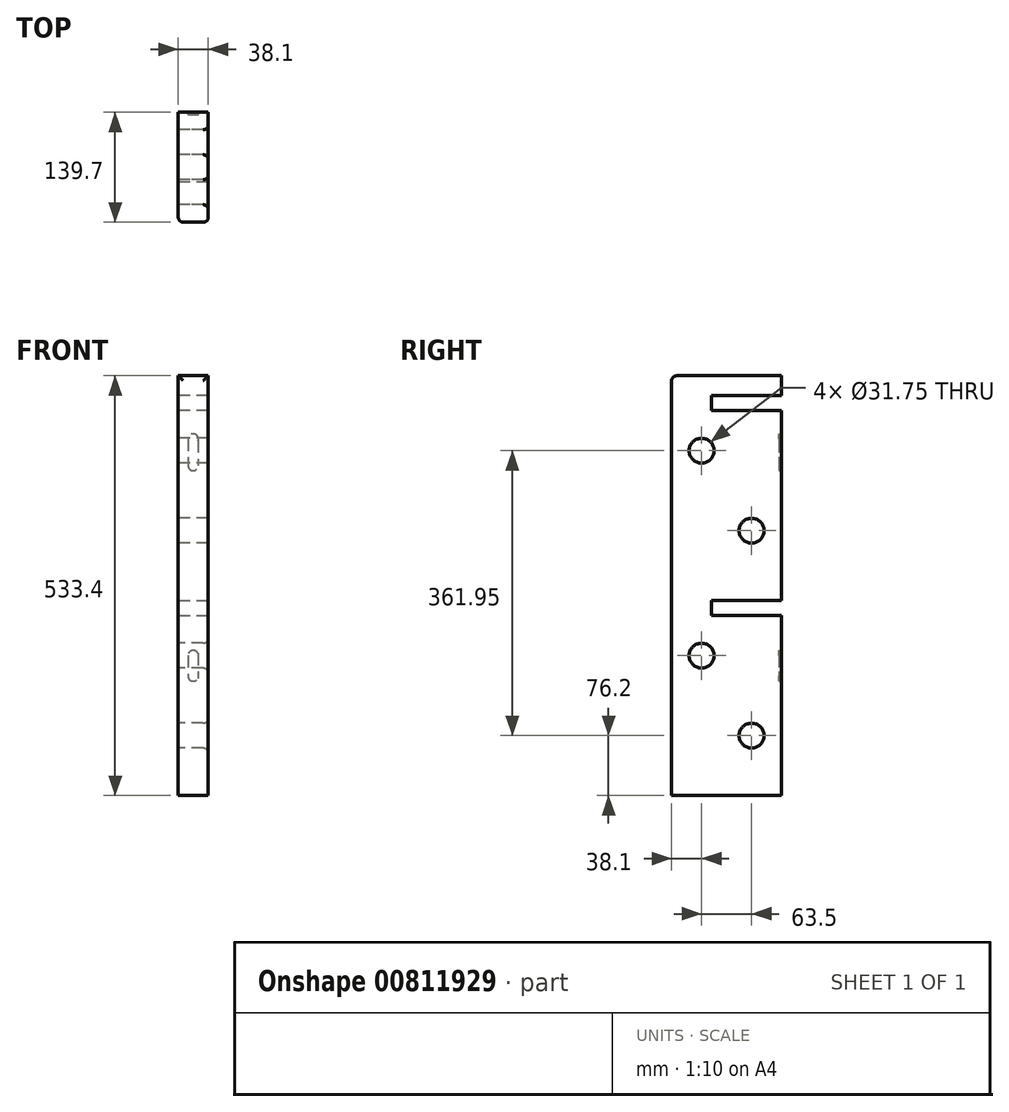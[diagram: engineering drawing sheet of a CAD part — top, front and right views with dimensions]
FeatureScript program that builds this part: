
annotation { "Feature Type Name" : "Feature", "Feature Type Description" : "" }
export const myFeature = defineFeature(function(context is Context, id is Id, definition is map)
    precondition{}
    {
        {
            var Q0;
            Q0=qCreatedBy(makeId("Front.planeOp"),FACE);
            var sketch = newSketch(context, id + "F0", { "sketchPlane" : qUnion([Q0])});
            skLineSegment(sketch, "E0.bottom", {"start": v(-19.05, 304.8) * mm, "end": v(19.05, 304.8) * mm});
            skLineSegment(sketch, "E0.top", {"start": v(-19.05, -304.8) * mm, "end": v(19.05, -304.8) * mm});
            skLineSegment(sketch, "E0.left", {"start": v(-19.05, 304.8) * mm, "end": v(-19.05, -304.8) * mm});
            skLineSegment(sketch, "E0.right", {"start": v(19.05, 304.8) * mm, "end": v(19.05, -304.8) * mm});
            skSolve(sketch);
        }
        {
            var Q0;
            Q0 = qSketchRegion(id + "F0", true);
            extrude(context, id + "F1", {"entities" : qUnion([Q0]), "depth" : 69.85 * mm, "offsetDistance" : 25.4 * mm, "hasSecondDirection" : true, "secondDirectionOppositeDirection" : true, "secondDirectionDepth" : 69.85 * mm});
        }
        {
            var Q0;
            Q0=makeQuery(id+"F1.opExtrude","SWEPT_FACE",FACE,{"disambiguationData":[OSD([sQuery(id+"F0.wireOp",EDGE,"E0.left")])]});
            var sketch = newSketch(context, id + "F2", { "sketchPlane" : qUnion([Q0])});
            skLineSegment(sketch, "E1.bottom", {"start": v(-69.85, 279.4) * mm, "end": v(19.05, 279.4) * mm});
            skLineSegment(sketch, "E1.top", {"start": v(-69.85, 260.35) * mm, "end": v(19.05, 260.35) * mm});
            skLineSegment(sketch, "E1.left", {"start": v(-69.85, 279.4) * mm, "end": v(-69.85, 260.35) * mm});
            skLineSegment(sketch, "E1.right", {"start": v(19.05, 279.4) * mm, "end": v(19.05, 260.35) * mm});
            skSolve(sketch);
        }
        {
            var Q0;
            Q0=makeQuery(id+"F2.imprint","IMPRINT",FACE,{"disambiguationData":[TD([[makeQuery(id+"F2.imprint","IMPRINT",EDGE,{"derivedFrom":sQuery(id+"F2.wireOp",EDGE,"E1.bottom")}),-1.0]])]});
            extrude(context, id + "F3", {"entities" : qUnion([Q0]), "operationType" : NewBodyOperationType.REMOVE, "oppositeDirection" : true, "depth" : 38.1 * mm, "offsetDistance" : 25.4 * mm});
        }
        {
            var Q0;
            Q0=makeQuery(id+"F1.opExtrude","SWEPT_FACE",FACE,{"disambiguationData":[OSD([sQuery(id+"F0.wireOp",EDGE,"E0.left")])]});
            var sketch = newSketch(context, id + "F4", { "sketchPlane" : qUnion([Q0])});
            skLineSegment(sketch, "E2", {"start": v(31.75, 304.8) * mm, "end": v(31.75, -304.8) * mm});
            skLineSegment(sketch, "E3", {"start": v(-31.75, 260.35) * mm, "end": v(-31.75, -304.8) * mm});
            skSolve(sketch);
        }
        {
            var Q0;
            {var subQ3=sQuery(id+"F4.wireOp",EDGE,"E2");Q0=makeQuery(id+"F4.imprint","IMPRINT",FACE,{"disambiguationData":[TD([[makeQuery(id+"F4.imprint","IMPRINT",EDGE,{"derivedFrom":subQ3}),-1.0]])]});}
            var sketch = newSketch(context, id + "F5", { "sketchPlane" : qUnion([Q0])});
            skCircle(sketch, "E4", {"center": v(31.75, 209.55) * mm, "radius": 15.88 * mm});
            skCircle(sketch, "E5", {"center": v(-31.75, 107.95) * mm, "radius": 15.88 * mm});
            skCircle(sketch, "E6", {"center": v(31.75, -50.8) * mm, "radius": 15.88 * mm});
            skCircle(sketch, "E7", {"center": v(-31.75, -152.4) * mm, "radius": 15.88 * mm});
            skSolve(sketch);
        }
        {
            var Q0;
            Q0 = qSketchRegion(id + "F5", true);
            extrude(context, id + "F6", {"entities" : qUnion([Q0]), "operationType" : NewBodyOperationType.REMOVE, "oppositeDirection" : true, "depth" : 50.8 * mm, "offsetDistance" : 25.4 * mm});
        }
        {
            var Q0;
            Q0=makeQuery(id+"F1.opExtrude","SWEPT_FACE",FACE,{"disambiguationData":[OSD([sQuery(id+"F0.wireOp",EDGE,"E0.right")])]});
            var sketch = newSketch(context, id + "F7", { "sketchPlane" : qUnion([Q0])});
            skLineSegment(sketch, "E8.bottom", {"start": v(69.85, 19.05) * mm, "end": v(-19.05, 19.05) * mm});
            skLineSegment(sketch, "E8.top", {"start": v(69.85, 0) * mm, "end": v(-19.05, 0) * mm});
            skLineSegment(sketch, "E8.left", {"start": v(69.85, 19.05) * mm, "end": v(69.85, 0) * mm});
            skLineSegment(sketch, "E8.right", {"start": v(-19.05, 19.05) * mm, "end": v(-19.05, 0) * mm});
            skLineSegment(sketch, "E9.bottom", {"start": v(69.85, -228.6) * mm, "end": v(-69.85, -228.6) * mm});
            skLineSegment(sketch, "E9.top", {"start": v(69.85, -304.8) * mm, "end": v(-69.85, -304.8) * mm});
            skLineSegment(sketch, "E9.left", {"start": v(69.85, -228.6) * mm, "end": v(69.85, -304.8) * mm});
            skLineSegment(sketch, "E9.right", {"start": v(-69.85, -228.6) * mm, "end": v(-69.85, -304.8) * mm});
            skSolve(sketch);
        }
        {
            var Q0;
            Q0 = qSketchRegion(id + "F7", true);
            extrude(context, id + "F8", {"entities" : qUnion([Q0]), "operationType" : NewBodyOperationType.REMOVE, "endBound" : BoundingType.UP_TO_NEXT, "oppositeDirection" : true, "depth" : 25.4 * mm, "offsetDistance" : 25.4 * mm});
        }
        {
            var Q0;
            Q0=makeQuery(id+"F6.boolean.opBoolean","COPY",EDGE,{"derivedFrom":makeQuery(id+"F6.opExtrude","CAP_EDGE",EDGE,{"disambiguationData":[OSD([sQuery(id+"F5.wireOp",EDGE,"E4")])],"isStart":true})});
            var Q1;
            Q1=makeQuery(id+"F6.boolean.opBoolean","COPY",EDGE,{"derivedFrom":makeQuery(id+"F6.opExtrude","CAP_EDGE",EDGE,{"disambiguationData":[OSD([sQuery(id+"F5.wireOp",EDGE,"E5")])],"isStart":true})});
            var Q2;
            Q2=makeQuery(id+"F6.boolean.opBoolean","INTERSECT",EDGE,{"derivedFrom":[makeQuery(id+"F1.opExtrude","SWEPT_FACE",FACE,{"disambiguationData":[OSD([sQuery(id+"F0.wireOp",EDGE,"E0.right")])]}),makeQuery(id+"F6.opExtrude","SWEPT_FACE",FACE,{"disambiguationData":[OSD([sQuery(id+"F5.wireOp",EDGE,"E6")])]})]});
            var Q3;
            Q3=makeQuery(id+"F6.boolean.opBoolean","INTERSECT",EDGE,{"derivedFrom":[makeQuery(id+"F1.opExtrude","SWEPT_FACE",FACE,{"disambiguationData":[OSD([sQuery(id+"F0.wireOp",EDGE,"E0.right")])]}),makeQuery(id+"F6.opExtrude","SWEPT_FACE",FACE,{"disambiguationData":[OSD([sQuery(id+"F5.wireOp",EDGE,"E7")])]})]});
            fillet(context, id + "F9", {"entities" : qUnion([Q0, Q1, Q2, Q3]), "radius" : 6.35 * mm, "tangentPropagation" : true, "allowEdgeOverflow" : false});
        }
        {
            var Q0;
            {var subQ0=sQuery(id+"F0.wireOp",EDGE,"E0.left");var subQ2=sQuery(id+"F0.wireOp",EDGE,"E0.right");var subQ4=makeQuery(id+"F3.opExtrude","SWEPT_FACE",FACE,{"disambiguationData":[OSD([sQuery(id+"F2.wireOp",EDGE,"E1.top")])]});var subQ5=sQuery(id+"F0.wireOp",EDGE,"E0.top");Q0=makeQuery(id+"F8.boolean.opBoolean","SPLIT",FACE,{"disambiguationData":[TD([makeQuery(id+"F3.boolean.opBoolean","COPY",FACE,{"derivedFrom":subQ4})])],"derivedFrom":makeQuery(id+"F3.boolean.opBoolean","SPLIT",FACE,{"disambiguationData":[TD([makeQuery(id+"F1.opExtrude","SWEPT_FACE",FACE,{"disambiguationData":[OSD([subQ5])]})])],"derivedFrom":makeQuery(id+"F1.opExtrude","CAP_FACE",FACE,{"disambiguationData":[OSD([sQuery(id+"F0.wireOp",EDGE,"E0.bottom"),subQ5,subQ0,subQ2])],"isStart":true})})});}
            var sketch = newSketch(context, id + "F10", { "sketchPlane" : qUnion([Q0])});
            skLineSegment(sketch, "E10.left", {"start": v(-6.17, 222.25) * mm, "end": v(-6.17, 190.5) * mm});
            skLineSegment(sketch, "E10.right", {"start": v(6.53, 224.4) * mm, "end": v(6.53, 190.5) * mm});
            skArc(sketch, "E11", {"start": v(6.53, 224.4) * mm, "mid": v(-1.1, 230.85) * mm, "end": v(-6.17, 222.25) * mm});
            skArc(sketch, "E12", {"start": v(-6.17, 190.5) * mm, "mid": v(0.18, 184.15) * mm, "end": v(6.53, 190.5) * mm});
            skLineSegment(sketch, "E13.left", {"start": v(-5.9, -48.05) * mm, "end": v(-5.9, -79.8) * mm});
            skLineSegment(sketch, "E13.right", {"start": v(6.8, -50.8) * mm, "end": v(6.8, -76.45) * mm});
            skArc(sketch, "E14", {"start": v(6.8, -50.8) * mm, "mid": v(1.55, -44.3) * mm, "end": v(-5.9, -48.05) * mm});
            skArc(sketch, "E15", {"start": v(-5.9, -79.8) * mm, "mid": v(1.73, -83.01) * mm, "end": v(6.8, -76.45) * mm});
            skSolve(sketch);
        }
        {
            var Q0;
            Q0 = qSketchRegion(id + "F10", true);
            extrude(context, id + "F11", {"entities" : qUnion([Q0]), "operationType" : NewBodyOperationType.REMOVE, "oppositeDirection" : true, "depth" : 3.17 * mm, "offsetDistance" : 25.4 * mm});
        }
        {
            var Q0;
            Q0=makeQuery(id+"F1.opExtrude","CAP_EDGE",EDGE,{"disambiguationData":[OSD([sQuery(id+"F0.wireOp",EDGE,"E0.right")])],"isStart":false});
            var Q1;
            Q1=makeQuery(id+"F1.opExtrude","CAP_EDGE",EDGE,{"disambiguationData":[OSD([sQuery(id+"F0.wireOp",EDGE,"E0.left")])],"isStart":false});
            var Q2;
            Q2=makeQuery(id+"F1.opExtrude","CAP_EDGE",EDGE,{"disambiguationData":[OSD([sQuery(id+"F0.wireOp",EDGE,"E0.bottom")])],"isStart":false});
            var Q3;
            Q3=makeQuery(id+"F8.boolean.opBoolean","COPY",EDGE,{"derivedFrom":makeQuery(id+"F8.opExtrude","SWEPT_EDGE",EDGE,{"disambiguationData":[OSD([sQuery(id+"F0.wireOp",EDGE,"E0.right"),sQuery(id+"F7.wireOp",EDGE,"E9.bottom"),sQuery(id+"F7.wireOp",EDGE,"E9.right")])]})});
            fillet(context, id + "F12", {"entities" : qUnion([Q0, Q1, Q2, Q3]), "radius" : 6.35 * mm, "tangentPropagation" : true, "allowEdgeOverflow" : false});
        }
    });
